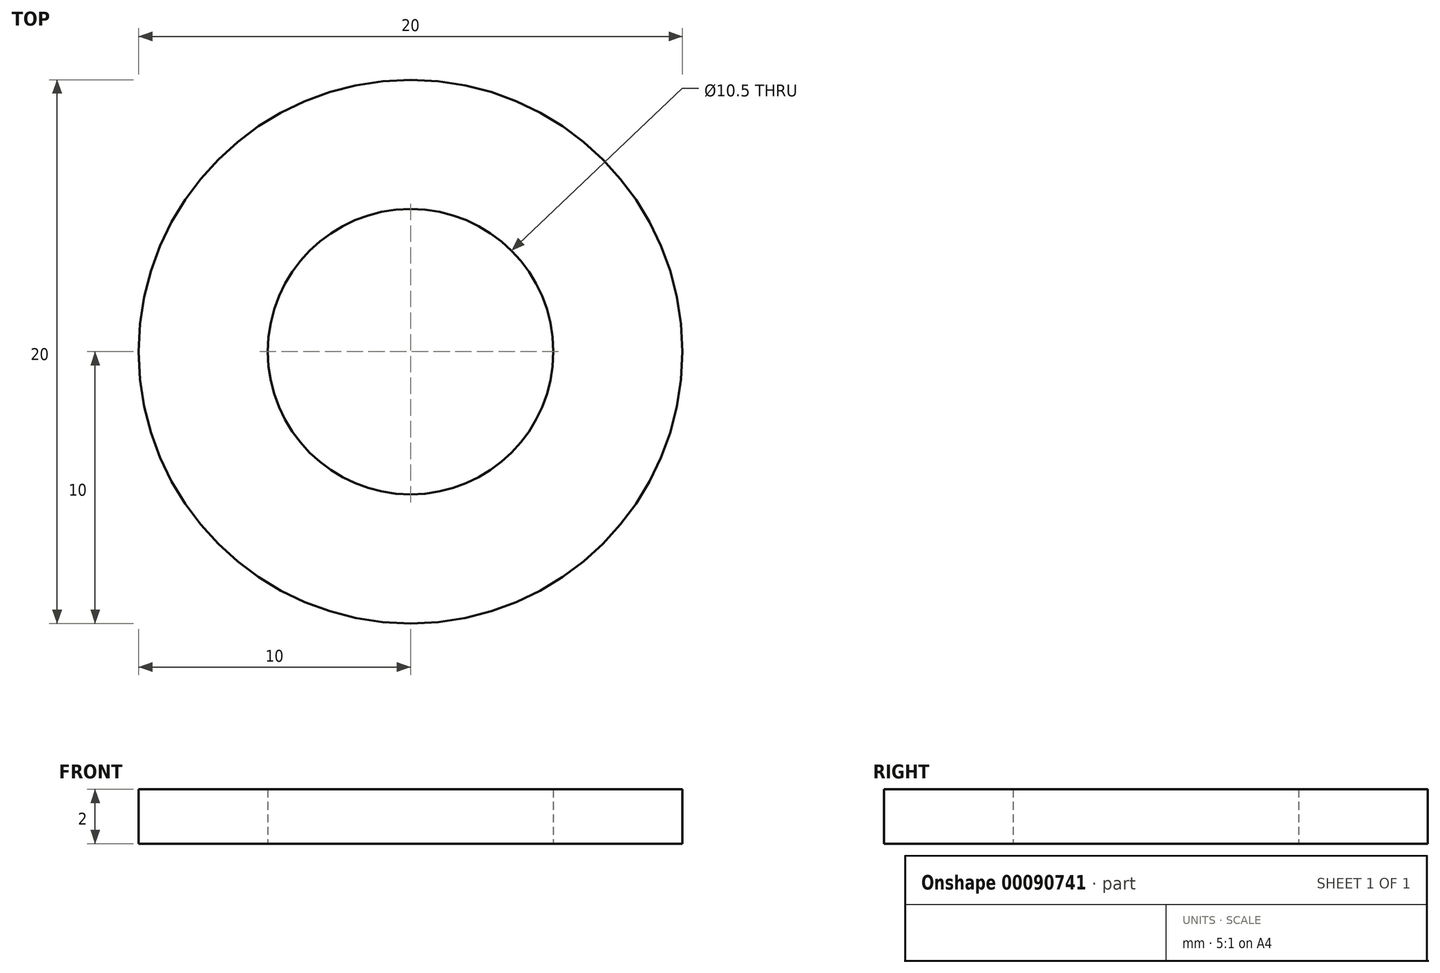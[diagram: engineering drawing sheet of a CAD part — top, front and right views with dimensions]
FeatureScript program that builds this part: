
annotation { "Feature Type Name" : "Feature", "Feature Type Description" : "" }
export const myFeature = defineFeature(function(context is Context, id is Id, definition is map)
    precondition{}
    {
        {
            var Q0;
            Q0=qCreatedBy(makeId("Top.planeOp"),FACE);
            var sketch = newSketch(context, id + "F0", { "sketchPlane" : qUnion([Q0])});
            skCircle(sketch, "E0", {"center": v(0, 0) * mm, "radius": 5.25 * mm});
            skCircle(sketch, "E1", {"center": v(0, 0) * mm, "radius": 10 * mm});
            skSolve(sketch);
        }
        {
            var Q0;
            Q0 = qSketchRegion(id + "F0", true);
            extrude(context, id + "F1", {"entities" : qUnion([Q0]), "endBound" : BoundingType.SYMMETRIC, "depth" : 2 * mm});
        }
    });
